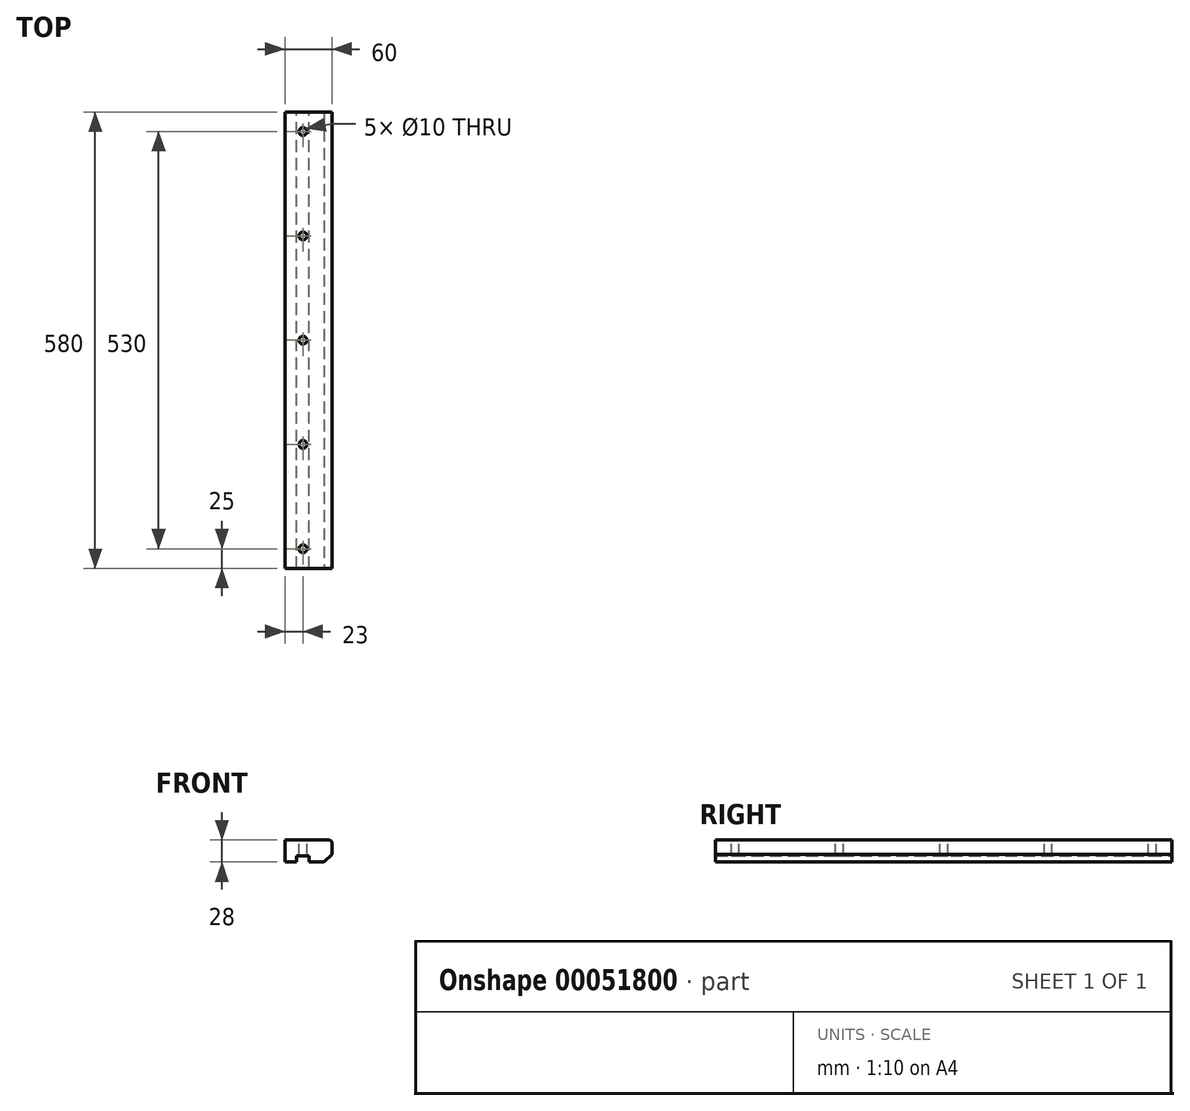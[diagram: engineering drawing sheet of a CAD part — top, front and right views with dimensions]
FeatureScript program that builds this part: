
annotation { "Feature Type Name" : "Feature", "Feature Type Description" : "" }
export const myFeature = defineFeature(function(context is Context, id is Id, definition is map)
    precondition{}
    {
        {
            var Q0;
            Q0=qCreatedBy(makeId("Front.planeOp"),FACE);
            var sketch = newSketch(context, id + "F0", { "sketchPlane" : qUnion([Q0])});
            skLineSegment(sketch, "E0.rect.bottom", {"start": v(30, 14) * mm, "end": v(-30, 14) * mm});
            skLineSegment(sketch, "E0.rect.top", {"start": v(30, -14) * mm, "end": v(-30, -14) * mm});
            skLineSegment(sketch, "E0.rect.left", {"start": v(30, 14) * mm, "end": v(30, -14) * mm});
            skLineSegment(sketch, "E0.rect.right", {"start": v(-30, 14) * mm, "end": v(-30, -14) * mm});
            skPoint(sketch, "E0.rect.middle", {"position": v(0, 0) * mm});
            skLineSegment(sketch, "E1", {"start": v(-30, -14) * mm, "end": v(-15, -14) * mm, "construction": true});
            skLineSegment(sketch, "E2", {"start": v(-15, -14) * mm, "end": v(-15, -6) * mm, "construction": true});
            skLineSegment(sketch, "E3", {"start": v(-15, -6) * mm, "end": v(1, -6) * mm});
            skLineSegment(sketch, "E4", {"start": v(1, -6) * mm, "end": v(1, -14) * mm, "construction": true});
            skLineSegment(sketch, "E5", {"start": v(1, -14) * mm, "end": v(30, -14) * mm, "construction": true});
            skLineSegment(sketch, "E6", {"start": v(-15, -14) * mm, "end": v(-15, -6) * mm});
            skLineSegment(sketch, "E7", {"start": v(1, -6) * mm, "end": v(1, -14) * mm});
            skSolve(sketch);
        }
        {
            var Q0;
            Q0=makeQuery(id+"F0.imprint","IMPRINT",FACE,{"disambiguationData":[TD([[makeQuery(id+"F0.imprint","IMPRINT",EDGE,{"derivedFrom":sQuery(id+"F0.wireOp",EDGE,"E0.rect.bottom")}),1.0]])]});
            extrude(context, id + "F1", {"entities" : qUnion([Q0]), "depth" : 580 * mm});
        }
        {
            var Q0;
            Q0=makeQuery(id+"F1.opExtrude","SWEPT_EDGE",EDGE,{"disambiguationData":[OSD([sQuery(id+"F0.wireOp",EDGE,"E0.rect.top"),sQuery(id+"F0.wireOp",EDGE,"E0.rect.left")])]});
            chamfer(context, id + "F2", {"entities" : qUnion([Q0]), "chamferType" : ChamferType.OFFSET_ANGLE, "width" : 10 * mm, "oppositeDirection" : false, "angle" : 45 * degree, "tangentPropagation" : true});
        }
        {
            var Q0;
            Q0=makeQuery(id+"F1.opExtrude","SWEPT_EDGE",EDGE,{"disambiguationData":[OSD([sQuery(id+"F0.wireOp",EDGE,"E0.rect.bottom"),sQuery(id+"F0.wireOp",EDGE,"E0.rect.left")])]});
            fillet(context, id + "F3", {"entities" : qUnion([Q0]), "radius" : 5 * mm, "rho" : 0.5, "crossSection" : FilletCrossSection.CONIC, "allowEdgeOverflow" : false});
        }
        {
            var Q0;
            Q0=makeQuery(id+"F1.opExtrude","SWEPT_FACE",FACE,{"disambiguationData":[OSD([sQuery(id+"F0.wireOp",EDGE,"E0.rect.bottom")])]});
            var sketch = newSketch(context, id + "F4", { "sketchPlane" : qUnion([Q0])});
            skLineSegment(sketch, "E8", {"start": v(-30, -580) * mm, "end": v(-7, -580) * mm, "construction": true});
            skLineSegment(sketch, "E9", {"start": v(-7, -580) * mm, "end": v(-7, -555) * mm, "construction": true});
            skLineSegment(sketch, "E10", {"start": v(-7, -555) * mm, "end": v(-7, -422.5) * mm, "construction": true});
            skLineSegment(sketch, "E11", {"start": v(-7, -422.5) * mm, "end": v(-7, -290) * mm, "construction": true});
            skLineSegment(sketch, "E12", {"start": v(-7, -290) * mm, "end": v(-7, -157.5) * mm, "construction": true});
            skLineSegment(sketch, "E13", {"start": v(-7, -157.5) * mm, "end": v(-7, -25) * mm, "construction": true});
            skCircle(sketch, "E14", {"center": v(-7, -555) * mm, "radius": 5 * mm});
            skCircle(sketch, "E15", {"center": v(-7, -422.5) * mm, "radius": 5 * mm});
            skCircle(sketch, "E16", {"center": v(-7, -290) * mm, "radius": 5 * mm});
            skCircle(sketch, "E17", {"center": v(-7, -157.5) * mm, "radius": 5 * mm});
            skCircle(sketch, "E18", {"center": v(-7, -25) * mm, "radius": 5 * mm});
            skSolve(sketch);
        }
        {
            var Q0;
            Q0=makeQuery(id+"F4.imprint","IMPRINT",FACE,{"disambiguationData":[TD([[makeQuery(id+"F4.imprint","IMPRINT",EDGE,{"derivedFrom":sQuery(id+"F4.wireOp",EDGE,"E18")}),1.0]])]});
            var Q1;
            Q1=makeQuery(id+"F4.imprint","IMPRINT",FACE,{"disambiguationData":[TD([[makeQuery(id+"F4.imprint","IMPRINT",EDGE,{"derivedFrom":sQuery(id+"F4.wireOp",EDGE,"E16")}),1.0]])]});
            var Q2;
            Q2=makeQuery(id+"F4.imprint","IMPRINT",FACE,{"disambiguationData":[TD([[makeQuery(id+"F4.imprint","IMPRINT",EDGE,{"derivedFrom":sQuery(id+"F4.wireOp",EDGE,"E17")}),1.0]])]});
            var Q3;
            Q3=makeQuery(id+"F4.imprint","IMPRINT",FACE,{"disambiguationData":[TD([[makeQuery(id+"F4.imprint","IMPRINT",EDGE,{"derivedFrom":sQuery(id+"F4.wireOp",EDGE,"E15")}),1.0]])]});
            var Q4;
            Q4=makeQuery(id+"F4.imprint","IMPRINT",FACE,{"disambiguationData":[TD([[makeQuery(id+"F4.imprint","IMPRINT",EDGE,{"derivedFrom":sQuery(id+"F4.wireOp",EDGE,"E14")}),1.0]])]});
            extrude(context, id + "F5", {"entities" : qUnion([Q0, Q1, Q2, Q3, Q4]), "operationType" : NewBodyOperationType.REMOVE, "endBound" : BoundingType.THROUGH_ALL, "oppositeDirection" : true, "depth" : 1.25 * mm});
        }
    });
